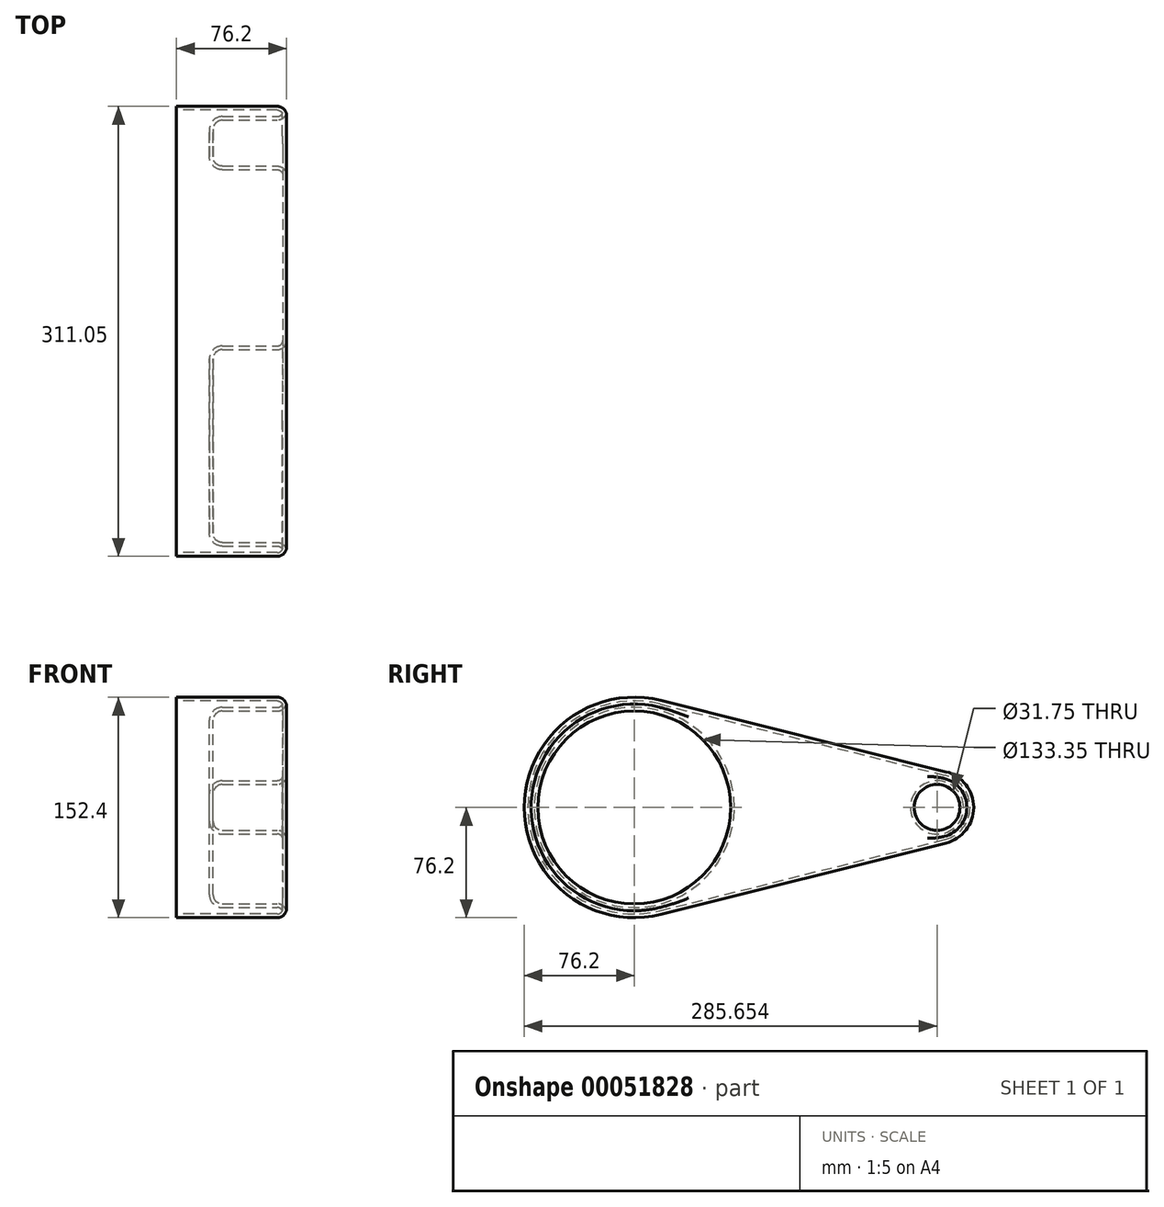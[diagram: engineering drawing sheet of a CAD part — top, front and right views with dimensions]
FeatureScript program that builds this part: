
annotation { "Feature Type Name" : "Feature", "Feature Type Description" : "" }
export const myFeature = defineFeature(function(context is Context, id is Id, definition is map)
    precondition{}
    {
        {
            var Q0;
            Q0=qCreatedBy(makeId("Right.planeOp"),FACE);
            var sketch = newSketch(context, id + "F0", { "sketchPlane" : qUnion([Q0])});
            skCircle(sketch, "E0", {"center": v(0, 0) * mm, "radius": 76.2 * mm});
            skCircle(sketch, "E1", {"center": v(209.45, 0) * mm, "radius": 25.4 * mm});
            skLineSegment(sketch, "E2", {"start": v(18.48, 73.92) * mm, "end": v(215.61, 24.64) * mm});
            skLineSegment(sketch, "E3", {"start": v(18.48, -73.92) * mm, "end": v(215.61, -24.64) * mm});
            skSolve(sketch);
        }
        {
            var Q0;
            {var subQ0=sQuery(id+"F0.wireOp",EDGE,"E2");Q0=makeQuery(id+"F0.imprint","IMPRINT",FACE,{"disambiguationData":[TD([[makeQuery(id+"F0.imprint","IMPRINT",EDGE,{"derivedFrom":subQ0}),-1.0]])]});}
            var Q1;
            {var subQ0=sQuery(id+"F0.wireOp",EDGE,"E0");var subQ1=makeQuery(id+"F0.imprint","INTERSECT",VERTEX,{"derivedFrom":[subQ0,sQuery(id+"F0.wireOp",EDGE,"E2")]});Q1=makeQuery(id+"F0.imprint","IMPRINT",FACE,{"disambiguationData":[TD([[makeQuery(id+"F0.imprint","IMPRINT",EDGE,{"disambiguationData":[TD([[subQ1,-1.0]])],"derivedFrom":subQ0}),1.0]])]});}
            var Q2;
            {var subQ0=sQuery(id+"F0.wireOp",EDGE,"E1");var subQ1=makeQuery(id+"F0.imprint","INTERSECT",VERTEX,{"derivedFrom":[subQ0,sQuery(id+"F0.wireOp",EDGE,"E2")]});Q2=makeQuery(id+"F0.imprint","IMPRINT",FACE,{"disambiguationData":[TD([[makeQuery(id+"F0.imprint","IMPRINT",EDGE,{"disambiguationData":[TD([[subQ1,-1.0]])],"derivedFrom":subQ0}),1.0]])]});}
            extrude(context, id + "F1", {"entities" : qUnion([Q0, Q1, Q2]), "depth" : 76.2 * mm});
        }
        {
            var Q0;
            Q0=makeQuery(id+"F1.opExtrude","CAP_FACE",FACE,{"disambiguationData":[OSD([sQuery(id+"F0.wireOp",EDGE,"E0"),sQuery(id+"F0.wireOp",EDGE,"E1"),sQuery(id+"F0.wireOp",EDGE,"E2"),sQuery(id+"F0.wireOp",EDGE,"E3")])],"isStart":false});
            var sketch = newSketch(context, id + "F2", { "sketchPlane" : qUnion([Q0])});
            skCircle(sketch, "E4", {"center": v(0, 0) * mm, "radius": 66.68 * mm});
            skCircle(sketch, "E5", {"center": v(209.45, 0) * mm, "radius": 15.88 * mm});
            skSolve(sketch);
        }
        {
            var Q0;
            Q0=makeQuery(id+"F2.imprint","IMPRINT",FACE,{"disambiguationData":[TD([[makeQuery(id+"F2.imprint","IMPRINT",EDGE,{"derivedFrom":sQuery(id+"F2.wireOp",EDGE,"E4")}),1.0]])]});
            var Q1;
            Q1=makeQuery(id+"F2.imprint","IMPRINT",FACE,{"disambiguationData":[TD([[makeQuery(id+"F2.imprint","IMPRINT",EDGE,{"derivedFrom":sQuery(id+"F2.wireOp",EDGE,"E5")}),1.0]])]});
            extrude(context, id + "F3", {"entities" : qUnion([Q0, Q1]), "operationType" : NewBodyOperationType.REMOVE, "oppositeDirection" : true, "depth" : 50.8 * mm});
        }
        {
            var Q0;
            Q0=makeQuery(id+"F1.opExtrude","CAP_FACE",FACE,{"disambiguationData":[OSD([sQuery(id+"F0.wireOp",EDGE,"E0"),sQuery(id+"F0.wireOp",EDGE,"E1"),sQuery(id+"F0.wireOp",EDGE,"E2"),sQuery(id+"F0.wireOp",EDGE,"E3")])],"isStart":false});
            var Q1;
            Q1=makeQuery(id+"F3.boolean.opBoolean","COPY",FACE,{"derivedFrom":makeQuery(id+"F3.opExtrude","SWEPT_FACE",FACE,{"disambiguationData":[OSD([sQuery(id+"F2.wireOp",EDGE,"E4")])]})});
            var Q2;
            Q2=makeQuery(id+"F3.boolean.opBoolean","COPY",FACE,{"derivedFrom":makeQuery(id+"F3.opExtrude","SWEPT_FACE",FACE,{"disambiguationData":[OSD([sQuery(id+"F2.wireOp",EDGE,"E5")])]})});
            fillet(context, id + "F4", {"entities" : qUnion([Q0, Q1, Q2]), "radius" : 6.35 * mm, "tangentPropagation" : true, "allowEdgeOverflow" : false});
        }
        {
            var Q0;
            Q0=makeQuery(id+"F1.opExtrude","CAP_FACE",FACE,{"disambiguationData":[OSD([sQuery(id+"F0.wireOp",EDGE,"E0"),sQuery(id+"F0.wireOp",EDGE,"E1"),sQuery(id+"F0.wireOp",EDGE,"E2"),sQuery(id+"F0.wireOp",EDGE,"E3")])],"isStart":true});
            shell(context, id + "F5", {"entities" : qUnion([Q0]), "thickness" : 2.54 * mm});
        }
    });
